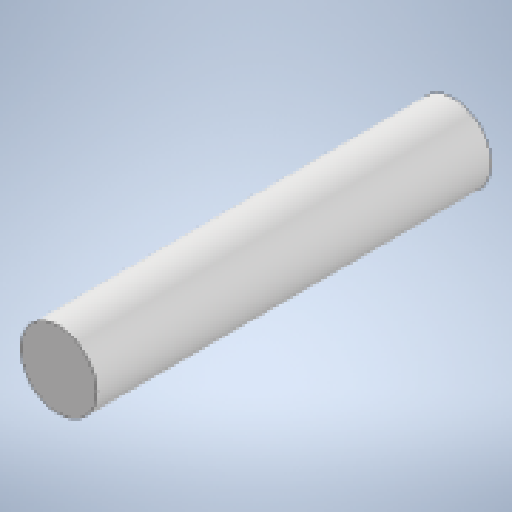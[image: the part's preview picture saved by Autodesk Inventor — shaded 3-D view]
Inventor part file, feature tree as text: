
AUTODESK INVENTOR PART (.ipt)
format: ipt  version: 2023 (Build 270158000, 158)  size: 133,120 bytes
history: native  units: in
note: dims shown in document units (in); Inventor stores cm internally (conversion verified against a paired STEP export)
features: extrude x1, sketch x1
ambient origin geometry x8: Origin, YZ Plane, XZ Plane, XY Plane, X Axis, Y Axis, Z Axis, Center Point
bodies: Solid1 (feature_tree)
feature tree (2):
  extrude  "Extrusion1"  Depth=1.1811in TaperAngle=0.0deg
  sketch  "Sketch1"  dims[d0=0.2283in d1=1.1811in d2=0.0in]
